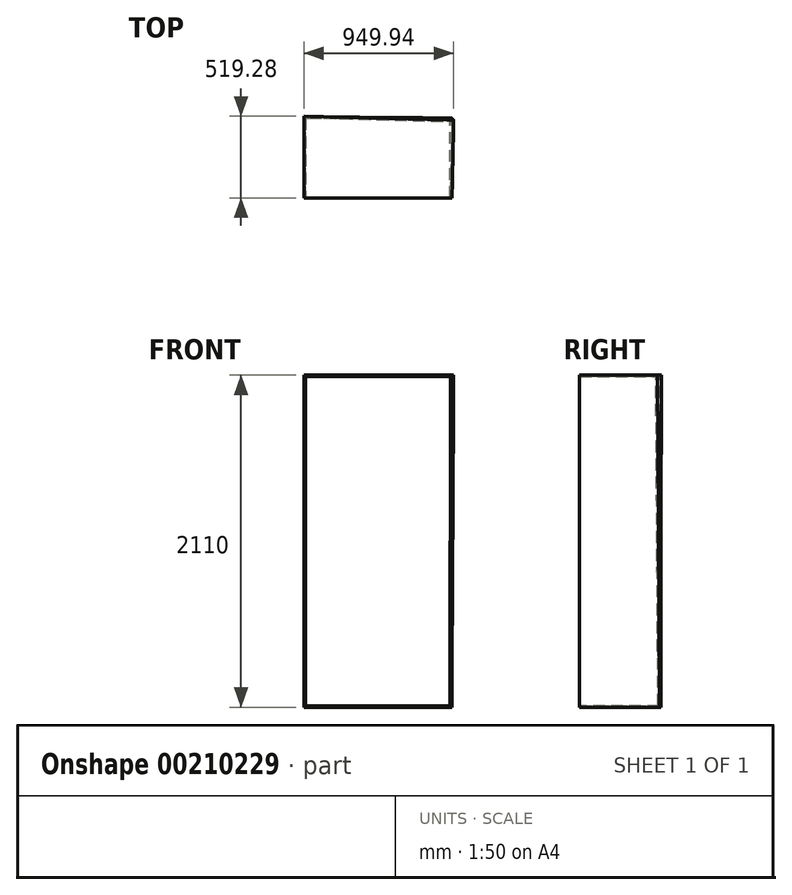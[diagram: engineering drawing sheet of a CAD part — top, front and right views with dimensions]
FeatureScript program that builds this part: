
annotation { "Feature Type Name" : "Feature", "Feature Type Description" : "" }
export const myFeature = defineFeature(function(context is Context, id is Id, definition is map)
    precondition{}
    {
        {
            var Q0;
            Q0=qCreatedBy(makeId("Top.planeOp"),FACE);
            var sketch = newSketch(context, id + "F0", { "sketchPlane" : qUnion([Q0])});
            skLineSegment(sketch, "E0", {"start": v(0, 0) * mm, "end": v(918, 0) * mm});
            skLineSegment(sketch, "E1", {"start": v(918, 0) * mm, "end": v(917.97, 498) * mm});
            skLineSegment(sketch, "E2", {"start": v(917.97, 498) * mm, "end": v(0, 505) * mm});
            skLineSegment(sketch, "E3", {"start": v(0, 505) * mm, "end": v(0, 0) * mm});
            skSolve(sketch);
        }
        {
            var Q0;
            Q0=makeQuery(id+"F0.imprint","IMPRINT",FACE,{"disambiguationData":[TD([[makeQuery(id+"F0.imprint","IMPRINT",EDGE,{"derivedFrom":sQuery(id+"F0.wireOp",EDGE,"E0")}),1.0]])]});
            cPlane(context, id + "F1", {"entities" : qUnion([Q0]), "cplaneType" : CPlaneType.OFFSET, "offset" : 2090 * mm, "width" : 150 * mm, "height" : 150 * mm});
        }
        {
            var Q0;
            Q0=qCreatedBy(id+"F1.planeOp",FACE);
            var sketch = newSketch(context, id + "F2", { "sketchPlane" : qUnion([Q0])});
            skLineSegment(sketch, "E4", {"start": v(0, 0) * mm, "end": v(0, 509) * mm});
            skLineSegment(sketch, "E5", {"start": v(0, 509) * mm, "end": v(929.69, 484.9) * mm});
            skLineSegment(sketch, "E6", {"start": v(929.69, 484.9) * mm, "end": v(920, 0) * mm});
            skLineSegment(sketch, "E7", {"start": v(920, 0) * mm, "end": v(0, 0) * mm});
            skSolve(sketch);
        }
        {
            var Q0;
            Q0=makeQuery(id+"F0.imprint","IMPRINT",FACE,{"disambiguationData":[TD([[makeQuery(id+"F0.imprint","IMPRINT",EDGE,{"derivedFrom":sQuery(id+"F0.wireOp",EDGE,"E0")}),1.0]])]});
            var Q1;
            Q1 = qSketchRegion(id + "F2", true);
            var Q2;
            Q2=makeQuery(id+"F0.imprint","IMPRINT",FACE,{"disambiguationData":[TD([[makeQuery(id+"F0.imprint","IMPRINT",EDGE,{"derivedFrom":sQuery(id+"F0.wireOp",EDGE,"E0")}),1.0]])]});
            var Q3;
            Q3=makeQuery(id+"F2.imprint","IMPRINT",FACE,{"disambiguationData":[TD([[makeQuery(id+"F2.imprint","IMPRINT",EDGE,{"derivedFrom":sQuery(id+"F2.wireOp",EDGE,"E4")}),-1.0]])]});
            loft(context, id + "F3", {"sheetProfilesArray" : [{ "sheetProfileEntities" : qUnion([Q0]) }, { "sheetProfileEntities" : qUnion([Q1]) }], "wireProfilesArray" : [{ "wireProfileEntities" : qUnion([Q2]) }, { "wireProfileEntities" : qUnion([Q3]) }]});
        }
        {
            var Q0;
            Q0=makeQuery(id+"F3.opLoft","SWEPT_FACE",FACE,{"disambiguationData":[OSD([sQuery(id+"F0.wireOp",EDGE,"E0"),sQuery(id+"F0.wireOp",EDGE,"E1"),sQuery(id+"F0.wireOp",EDGE,"E3"),sQuery(id+"F2.wireOp",EDGE,"E4"),sQuery(id+"F2.wireOp",EDGE,"E6"),sQuery(id+"F2.wireOp",EDGE,"E7")])]});
            shell(context, id + "F4", {"entities" : qUnion([Q0]), "thickness" : 10 * mm, "oppositeDirection" : true});
        }
    });
